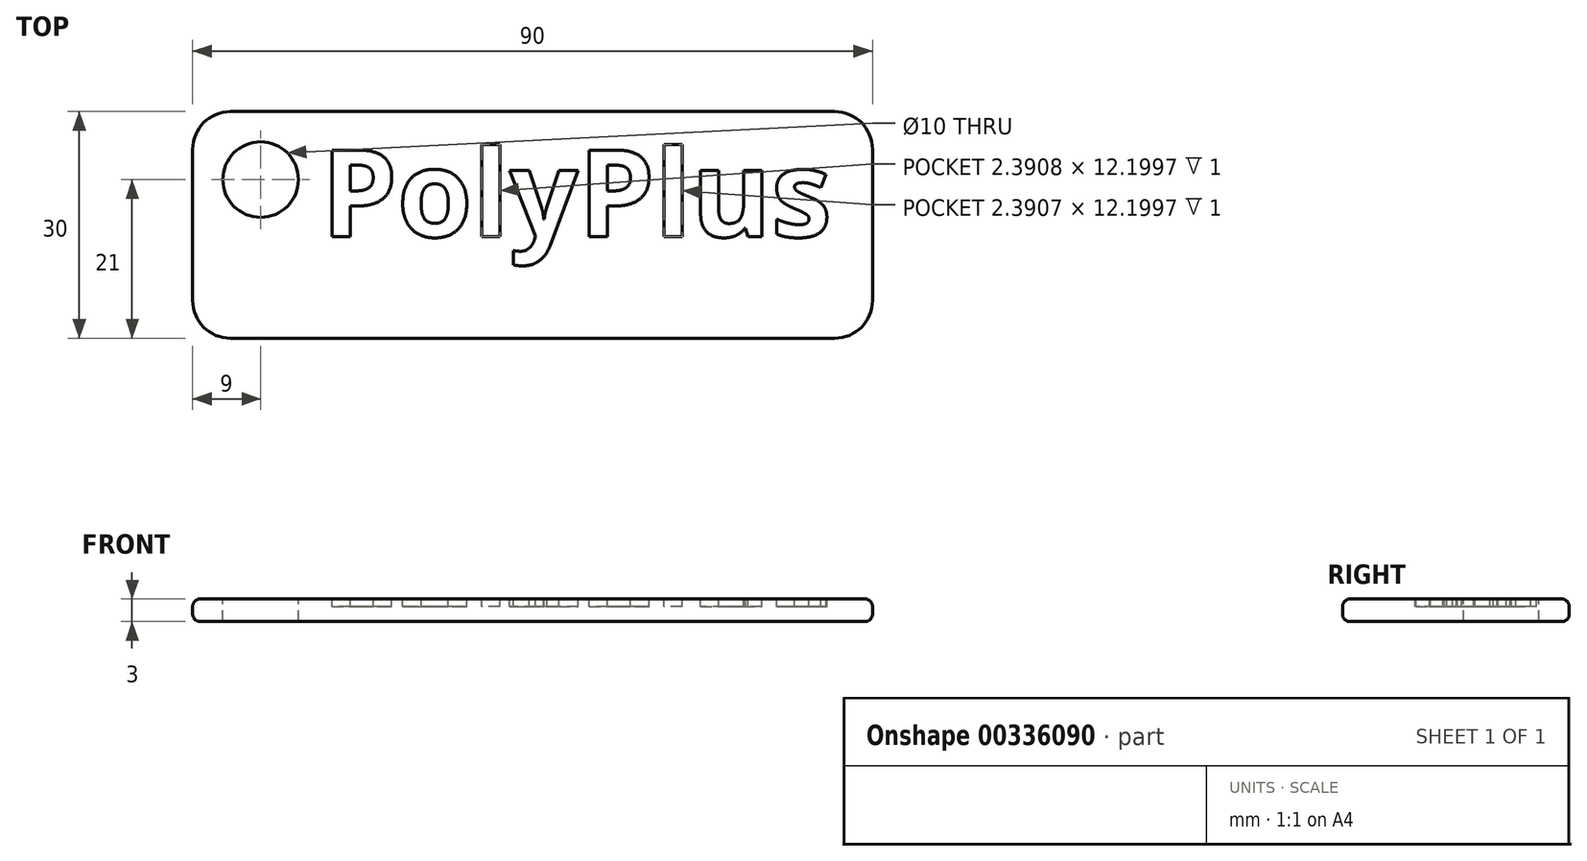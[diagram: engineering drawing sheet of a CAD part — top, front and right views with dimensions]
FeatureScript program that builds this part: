
annotation { "Feature Type Name" : "Feature", "Feature Type Description" : "" }
export const myFeature = defineFeature(function(context is Context, id is Id, definition is map)
    precondition{}
    {
        {
            var Q0;
            Q0=qCreatedBy(makeId("Top.planeOp"),FACE);
            var sketch = newSketch(context, id + "F0", { "sketchPlane" : qUnion([Q0])});
            skLineSegment(sketch, "E0.bottom", {"start": v(-45, 15) * mm, "end": v(45, 15) * mm});
            skLineSegment(sketch, "E0.top", {"start": v(-45, -15) * mm, "end": v(45, -15) * mm});
            skLineSegment(sketch, "E0.left", {"start": v(-45, 15) * mm, "end": v(-45, -15) * mm});
            skLineSegment(sketch, "E0.right", {"start": v(45, 15) * mm, "end": v(45, -15) * mm});
            skLineSegment(sketch, "E1", {"start": v(-45, 15) * mm, "end": v(45, -15) * mm, "construction": true});
            skSolve(sketch);
        }
        {
            var Q0;
            Q0=makeQuery(id+"F0.imprint","IMPRINT",FACE,{"disambiguationData":[TD([[makeQuery(id+"F0.imprint","IMPRINT",EDGE,{"derivedFrom":sQuery(id+"F0.wireOp",EDGE,"E0.bottom")}),-1.0]])]});
            extrude(context, id + "F1", {"entities" : qUnion([Q0]), "depth" : 3 * mm});
        }
        {
            var Q0;
            Q0=makeQuery(id+"F1.opExtrude","CAP_FACE",FACE,{"disambiguationData":[OSD([sQuery(id+"F0.wireOp",EDGE,"E0.bottom"),sQuery(id+"F0.wireOp",EDGE,"E0.top"),sQuery(id+"F0.wireOp",EDGE,"E0.left"),sQuery(id+"F0.wireOp",EDGE,"E0.right")])],"isStart":false});
            var Q1;
            Q1=makeQuery(id+"F1.opExtrude","CAP_FACE",FACE,{"disambiguationData":[OSD([sQuery(id+"F0.wireOp",EDGE,"E0.bottom"),sQuery(id+"F0.wireOp",EDGE,"E0.top"),sQuery(id+"F0.wireOp",EDGE,"E0.left"),sQuery(id+"F0.wireOp",EDGE,"E0.right")])],"isStart":true});
            fillet(context, id + "F2", {"entities" : qUnion([Q0, Q1]), "radius" : 1 * mm, "tangentPropagation" : true, "allowEdgeOverflow" : false});
        }
        {
            var Q0;
            Q0=makeQuery(id+"F1.opExtrude","SWEPT_EDGE",EDGE,{"disambiguationData":[OSD([sQuery(id+"F0.wireOp",EDGE,"E0.top"),sQuery(id+"F0.wireOp",EDGE,"E0.right")])]});
            var Q1;
            Q1=makeQuery(id+"F1.opExtrude","SWEPT_EDGE",EDGE,{"disambiguationData":[OSD([sQuery(id+"F0.wireOp",EDGE,"E0.bottom"),sQuery(id+"F0.wireOp",EDGE,"E0.right")])]});
            var Q2;
            Q2=makeQuery(id+"F1.opExtrude","SWEPT_EDGE",EDGE,{"disambiguationData":[OSD([sQuery(id+"F0.wireOp",EDGE,"E0.bottom"),sQuery(id+"F0.wireOp",EDGE,"E0.left")])]});
            var Q3;
            Q3=makeQuery(id+"F1.opExtrude","SWEPT_EDGE",EDGE,{"disambiguationData":[OSD([sQuery(id+"F0.wireOp",EDGE,"E0.top"),sQuery(id+"F0.wireOp",EDGE,"E0.left")])]});
            fillet(context, id + "F3", {"entities" : qUnion([Q0, Q1, Q2, Q3]), "radius" : 5 * mm, "tangentPropagation" : true, "allowEdgeOverflow" : false});
        }
        {
            var Q0;
            {var subQ0=sQuery(id+"F0.wireOp",EDGE,"E0.left");var subQ2=sQuery(id+"F0.wireOp",EDGE,"E0.bottom");var subQ4=sQuery(id+"F0.wireOp",EDGE,"E0.right");var subQ6=sQuery(id+"F0.wireOp",EDGE,"E0.top");Q0=makeQuery(id+"FmQCBBX3Ub0qneL_1.boolean.opBoolean","SPLIT",FACE,{"disambiguationData":[TD([makeQuery(id+"FmQCBBX3Ub0qneL_1.opExtrude","SWEPT_FACE",FACE,{"disambiguationData":[OSD([sQuery(id+"FOCoeRmDbjhRCuz_1.wireOp",EDGE,"4a1fb44a-e7be-4e23-9449-000d953c446c.sketch_text.stroke-0")])]})])],"derivedFrom":makeQuery(id+"F1.opExtrude","CAP_FACE",FACE,{"disambiguationData":[OSD([subQ2,subQ6,subQ0,subQ4])],"isStart":false})});}
            var sketch = newSketch(context, id + "F4", { "sketchPlane" : qUnion([Q0])});
            skCircle(sketch, "E2", {"center": v(-36, 6) * mm, "radius": 5 * mm});
            skSolve(sketch);
        }
        {
            var Q0;
            Q0=qSketchRegion(id+"F4",true);
            extrude(context, id + "F5", {"entities" : qUnion([Q0]), "operationType" : NewBodyOperationType.REMOVE, "oppositeDirection" : true, "depth" : 3 * mm});
        }
        {
            var Q0;
            Q0=makeQuery(id+"F1.opExtrude","CAP_FACE",FACE,{"disambiguationData":[OSD([sQuery(id+"F0.wireOp",EDGE,"E0.bottom"),sQuery(id+"F0.wireOp",EDGE,"E0.top"),sQuery(id+"F0.wireOp",EDGE,"E0.left"),sQuery(id+"F0.wireOp",EDGE,"E0.right")])],"isStart":false});
            var sketch = newSketch(context, id + "F6", { "sketchPlane" : qUnion([Q0])});
            skText(sketch, "E3", { "text": "PolyPlus", "fontName": "OpenSans-Bold.ttf"});
            const initialGuessF6  = {"E3": [-0.028, -0.00156, 1, 0, 0.01156]};
            skSetInitialGuess(sketch, initialGuessF6);
            skSolve(sketch);
        }
        {
            var Q0;
            Q0=qSketchRegion(id+"F6",true);
            extrude(context, id + "F7", {"entities" : qUnion([Q0]), "operationType" : NewBodyOperationType.REMOVE, "oppositeDirection" : true, "depth" : 1 * mm});
        }
    });
